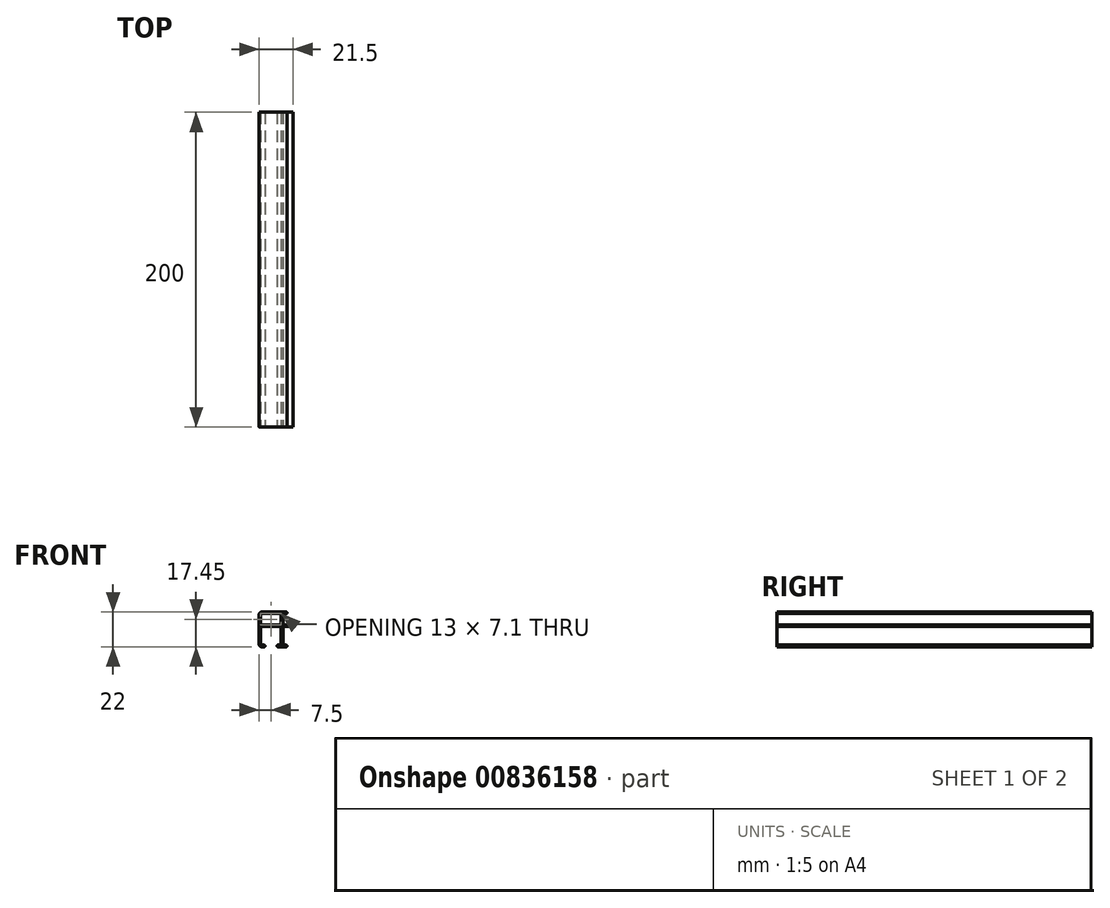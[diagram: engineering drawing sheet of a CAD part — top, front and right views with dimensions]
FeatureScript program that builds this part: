
annotation { "Feature Type Name" : "Feature", "Feature Type Description" : "" }
export const myFeature = defineFeature(function(context is Context, id is Id, definition is map)
    precondition{}
    {
        {
            var Q0;
            Q0=qCreatedBy(makeId("Front.planeOp"),FACE);
            var sketch = newSketch(context, id + "F0", { "sketchPlane" : qUnion([Q0])});
            skLineSegment(sketch, "E0", {"start": v(0, 0) * mm, "end": v(0, 29.04) * mm, "construction": true});
            skLineSegment(sketch, "E1.bottom", {"start": v(0, 22) * mm, "end": v(-21.5, 22) * mm, "construction": true});
            skLineSegment(sketch, "E1.top", {"start": v(-18.4, 0) * mm, "end": v(-21.5, 0) * mm, "construction": true});
            skLineSegment(sketch, "E1.left", {"start": v(0, 22) * mm, "end": v(0, 0) * mm, "construction": true});
            skLineSegment(sketch, "E1.right", {"start": v(-21.5, 22) * mm, "end": v(-21.5, 0) * mm, "construction": true});
            skLineSegment(sketch, "E2", {"start": v(-4.4, 22) * mm, "end": v(-20, 22) * mm});
            skLineSegment(sketch, "E3", {"start": v(-20, 0) * mm, "end": v(-17.95, 0) * mm});
            skLineSegment(sketch, "E4", {"start": v(-17.9, 0.5) * mm, "end": v(-17.9, 0.5) * mm});
            skLineSegment(sketch, "E5", {"start": v(-18.4, 1) * mm, "end": v(-20, 1) * mm});
            skLineSegment(sketch, "E6", {"start": v(-20.5, 1.5) * mm, "end": v(-20.5, 12.4) * mm});
            skLineSegment(sketch, "E7", {"start": v(-20, 12.9) * mm, "end": v(-8, 12.9) * mm});
            skLineSegment(sketch, "E8", {"start": v(-7.5, 12.4) * mm, "end": v(-7.5, 1.5) * mm});
            skLineSegment(sketch, "E9", {"start": v(-8, 1) * mm, "end": v(-9.6, 1) * mm});
            skLineSegment(sketch, "E10", {"start": v(-10.1, 0.5) * mm, "end": v(-10.1, 0.5) * mm});
            skLineSegment(sketch, "E11", {"start": v(-9.6, 0) * mm, "end": v(-4.4, 0) * mm});
            skLineSegment(sketch, "E12", {"start": v(-3.9, 0.5) * mm, "end": v(-3.9, 0.5) * mm});
            skLineSegment(sketch, "E13", {"start": v(-4.4, 1) * mm, "end": v(-6, 1) * mm});
            skLineSegment(sketch, "E14", {"start": v(-6.5, 1.5) * mm, "end": v(-6.5, 12.4) * mm});
            skLineSegment(sketch, "E15", {"start": v(-6, 12.9) * mm, "end": v(0, 12.9) * mm});
            skLineSegment(sketch, "E16", {"start": v(0, 12.9) * mm, "end": v(0, 13.9) * mm});
            skLineSegment(sketch, "E17", {"start": v(0, 13.9) * mm, "end": v(-6, 13.9) * mm});
            skLineSegment(sketch, "E18", {"start": v(-6.5, 14.4) * mm, "end": v(-6.5, 20.5) * mm});
            skLineSegment(sketch, "E19", {"start": v(-6, 21) * mm, "end": v(-4.4, 21) * mm});
            skLineSegment(sketch, "E20", {"start": v(-3.9, 21.5) * mm, "end": v(-3.9, 21.5) * mm});
            skLineSegment(sketch, "E21.bottom", {"start": v(-20, 13.9) * mm, "end": v(-8, 13.9) * mm});
            skLineSegment(sketch, "E21.top", {"start": v(-20, 21) * mm, "end": v(-8, 21) * mm});
            skLineSegment(sketch, "E21.left", {"start": v(-20.5, 14.4) * mm, "end": v(-20.5, 20.5) * mm});
            skLineSegment(sketch, "E21.right", {"start": v(-7.5, 14.4) * mm, "end": v(-7.5, 20.5) * mm});
            skLineSegment(sketch, "E22", {"start": v(-21.5, 20.5) * mm, "end": v(-21.5, 1.5) * mm});
            skLineSegment(sketch, "E23", {"start": v(-14, 12.9) * mm, "end": v(-14, 0) * mm, "construction": true});
            skPoint(sketch, "E24.visualSharp", {"position": v(-20.5, 21) * mm});
            skArc(sketch, "E24.filletArc", {"start": v(-20, 21) * mm, "mid": v(-20.35, 20.85) * mm, "end": v(-20.5, 20.5) * mm});
            skPoint(sketch, "E25.visualSharp", {"position": v(-7.5, 21) * mm});
            skArc(sketch, "E25.filletArc", {"start": v(-7.5, 20.5) * mm, "mid": v(-7.65, 20.85) * mm, "end": v(-8, 21) * mm});
            skPoint(sketch, "E26.visualSharp", {"position": v(-6.5, 21) * mm});
            skArc(sketch, "E26.filletArc", {"start": v(-6, 21) * mm, "mid": v(-6.35, 20.85) * mm, "end": v(-6.5, 20.5) * mm});
            skPoint(sketch, "E27.visualSharp", {"position": v(-20.5, 13.9) * mm});
            skArc(sketch, "E27.filletArc", {"start": v(-20.5, 14.4) * mm, "mid": v(-20.35, 14.05) * mm, "end": v(-20, 13.9) * mm});
            skPoint(sketch, "E28.visualSharp", {"position": v(-7.5, 13.9) * mm});
            skArc(sketch, "E28.filletArc", {"start": v(-8, 13.9) * mm, "mid": v(-7.65, 14.05) * mm, "end": v(-7.5, 14.4) * mm});
            skPoint(sketch, "E29.visualSharp", {"position": v(-6.5, 13.9) * mm});
            skArc(sketch, "E29.filletArc", {"start": v(-6.5, 14.4) * mm, "mid": v(-6.35, 14.05) * mm, "end": v(-6, 13.9) * mm});
            skPoint(sketch, "E30.visualSharp", {"position": v(-6.5, 12.9) * mm});
            skArc(sketch, "E30.filletArc", {"start": v(-6, 12.9) * mm, "mid": v(-6.35, 12.75) * mm, "end": v(-6.5, 12.4) * mm});
            skPoint(sketch, "E31.visualSharp", {"position": v(-7.5, 12.9) * mm});
            skArc(sketch, "E31.filletArc", {"start": v(-7.5, 12.4) * mm, "mid": v(-7.65, 12.75) * mm, "end": v(-8, 12.9) * mm});
            skPoint(sketch, "E32.visualSharp", {"position": v(-20.5, 12.9) * mm});
            skArc(sketch, "E32.filletArc", {"start": v(-20, 12.9) * mm, "mid": v(-20.35, 12.75) * mm, "end": v(-20.5, 12.4) * mm});
            skPoint(sketch, "E33.visualSharp", {"position": v(-20.5, 1) * mm});
            skArc(sketch, "E33.filletArc", {"start": v(-20.5, 1.5) * mm, "mid": v(-20.35, 1.15) * mm, "end": v(-20, 1) * mm});
            skPoint(sketch, "E34.visualSharp", {"position": v(-17.9, 1) * mm});
            skArc(sketch, "E34.filletArc", {"start": v(-17.9, 0.5) * mm, "mid": v(-18.05, 0.85) * mm, "end": v(-18.4, 1) * mm});
            skArc(sketch, "E35.filletArc", {"start": v(-18.4, 0) * mm, "mid": v(-18.05, 0.15) * mm, "end": v(-17.9, 0.5) * mm});
            skPoint(sketch, "E36.visualSharp", {"position": v(-10.1, 1) * mm});
            skArc(sketch, "E36.filletArc", {"start": v(-9.6, 1) * mm, "mid": v(-9.95, 0.85) * mm, "end": v(-10.1, 0.5) * mm});
            skPoint(sketch, "E37.visualSharp", {"position": v(-7.5, 1) * mm});
            skArc(sketch, "E37.filletArc", {"start": v(-8, 1) * mm, "mid": v(-7.65, 1.15) * mm, "end": v(-7.5, 1.5) * mm});
            skPoint(sketch, "E38.visualSharp", {"position": v(-6.5, 1) * mm});
            skArc(sketch, "E38.filletArc", {"start": v(-6.5, 1.5) * mm, "mid": v(-6.35, 1.15) * mm, "end": v(-6, 1) * mm});
            skPoint(sketch, "E39.visualSharp", {"position": v(-3.9, 1) * mm});
            skArc(sketch, "E39.filletArc", {"start": v(-3.9, 0.5) * mm, "mid": v(-4.05, 0.85) * mm, "end": v(-4.4, 1) * mm});
            skPoint(sketch, "E40.visualSharp", {"position": v(-10.1, 0) * mm});
            skArc(sketch, "E40.filletArc", {"start": v(-10.1, 0.5) * mm, "mid": v(-9.95, 0.15) * mm, "end": v(-9.6, 0) * mm});
            skPoint(sketch, "E41.visualSharp", {"position": v(-3.9, 0) * mm});
            skArc(sketch, "E41.filletArc", {"start": v(-4.4, 0) * mm, "mid": v(-4.05, 0.15) * mm, "end": v(-3.9, 0.5) * mm});
            skPoint(sketch, "E42.visualSharp", {"position": v(-3.9, 21) * mm});
            skArc(sketch, "E42.filletArc", {"start": v(-4.4, 21) * mm, "mid": v(-4.05, 21.15) * mm, "end": v(-3.9, 21.5) * mm});
            skPoint(sketch, "E43.visualSharp", {"position": v(-3.9, 22) * mm});
            skArc(sketch, "E43.filletArc", {"start": v(-3.9, 21.5) * mm, "mid": v(-4.05, 21.85) * mm, "end": v(-4.4, 22) * mm});
            skPoint(sketch, "E44.visualSharp", {"position": v(-21.5, 22) * mm});
            skArc(sketch, "E44.filletArc", {"start": v(-20, 22) * mm, "mid": v(-21.06, 21.56) * mm, "end": v(-21.5, 20.5) * mm});
            skPoint(sketch, "E45.visualSharp", {"position": v(-21.5, 0) * mm});
            skArc(sketch, "E45.filletArc", {"start": v(-21.5, 1.5) * mm, "mid": v(-21.06, 0.44) * mm, "end": v(-20, 0) * mm});
            skSolve(sketch);
        }
        {
            var Q0;
            Q0 = qSketchRegion(id + "F0", true);
            extrude(context, id + "F1", {"entities" : qUnion([Q0]), "oppositeDirection" : true, "depth" : 200 * mm, "offsetDistance" : 25 * mm});
        }
    });
